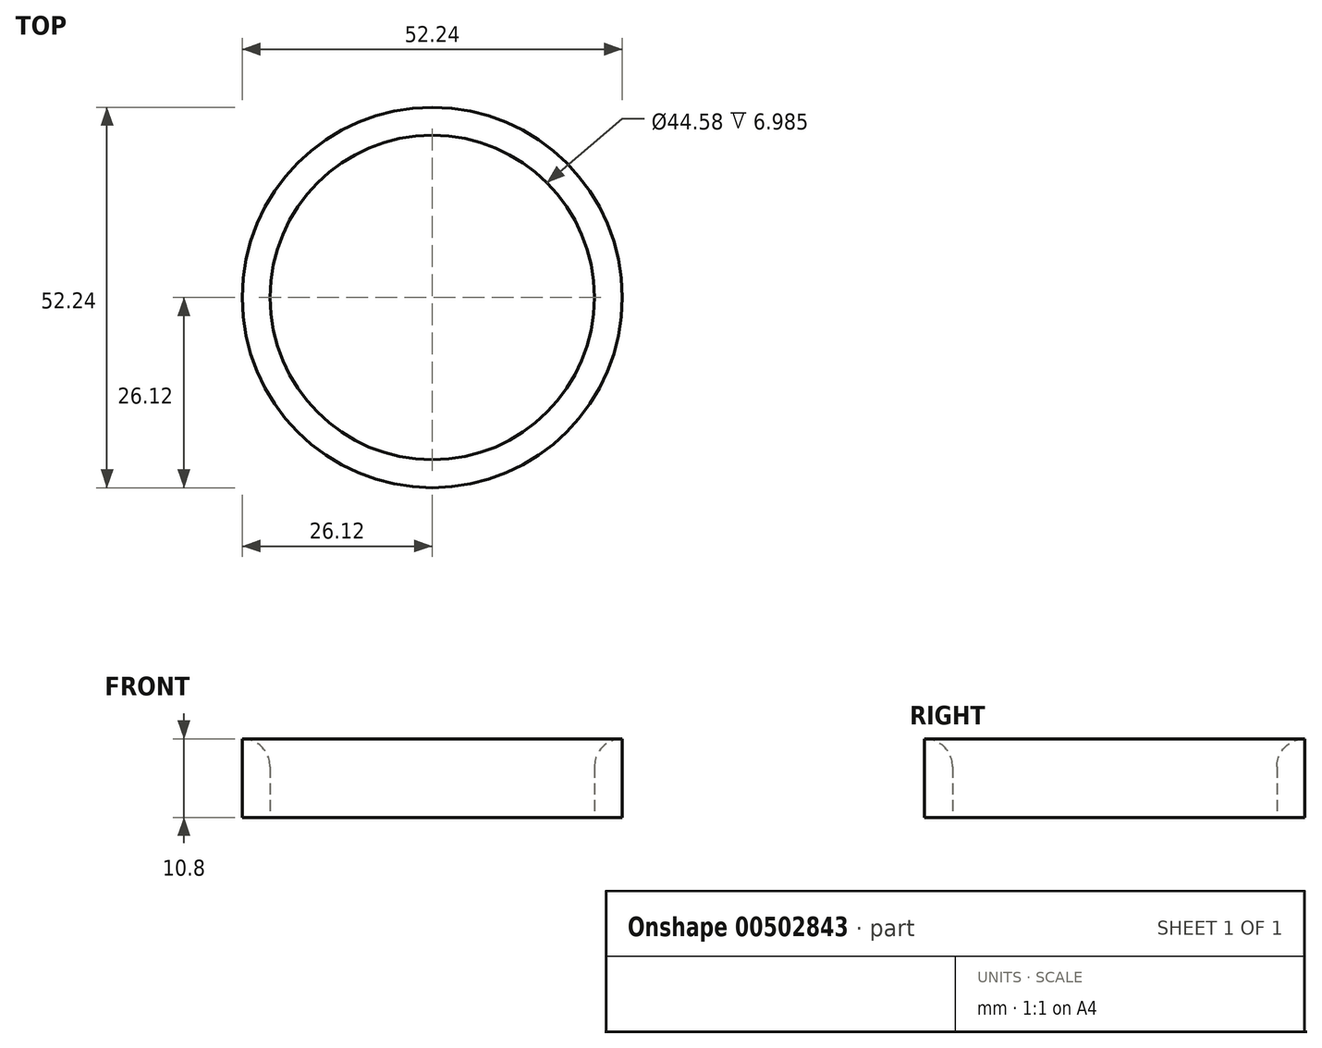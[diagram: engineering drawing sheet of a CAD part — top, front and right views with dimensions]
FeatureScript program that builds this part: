
annotation { "Feature Type Name" : "Feature", "Feature Type Description" : "" }
export const myFeature = defineFeature(function(context is Context, id is Id, definition is map)
    precondition{}
    {
        {
            var Q0;
            Q0=qCreatedBy(makeId("Top.planeOp"),FACE);
            var sketch = newSketch(context, id + "F0", { "sketchPlane" : qUnion([Q0])});
            skCircle(sketch, "E0", {"center": v(0, 0) * mm, "radius": 22.29 * mm});
            skCircle(sketch, "E1", {"center": v(0, 0) * mm, "radius": 26.12 * mm});
            skSolve(sketch);
        }
        {
            var Q0;
            Q0=makeQuery(id+"F0.imprint","IMPRINT",FACE,{"disambiguationData":[TD([[makeQuery(id+"F0.imprint","IMPRINT",EDGE,{"derivedFrom":sQuery(id+"F0.wireOp",EDGE,"E0")}),-1.0]])]});
            extrude(context, id + "F1", {"entities" : qUnion([Q0]), "depth" : 10.8 * mm, "offsetDistance" : 25.4 * mm});
        }
        {
            var Q0;
            Q0=makeQuery(id+"F1.opExtrude","CAP_EDGE",EDGE,{"disambiguationData":[OSD([sQuery(id+"F0.wireOp",EDGE,"E0")])],"isStart":false});
            fillet(context, id + "F2", {"entities" : qUnion([Q0]), "radius" : 3.8 * mm, "tangentPropagation" : true, "allowEdgeOverflow" : false});
        }
    });
